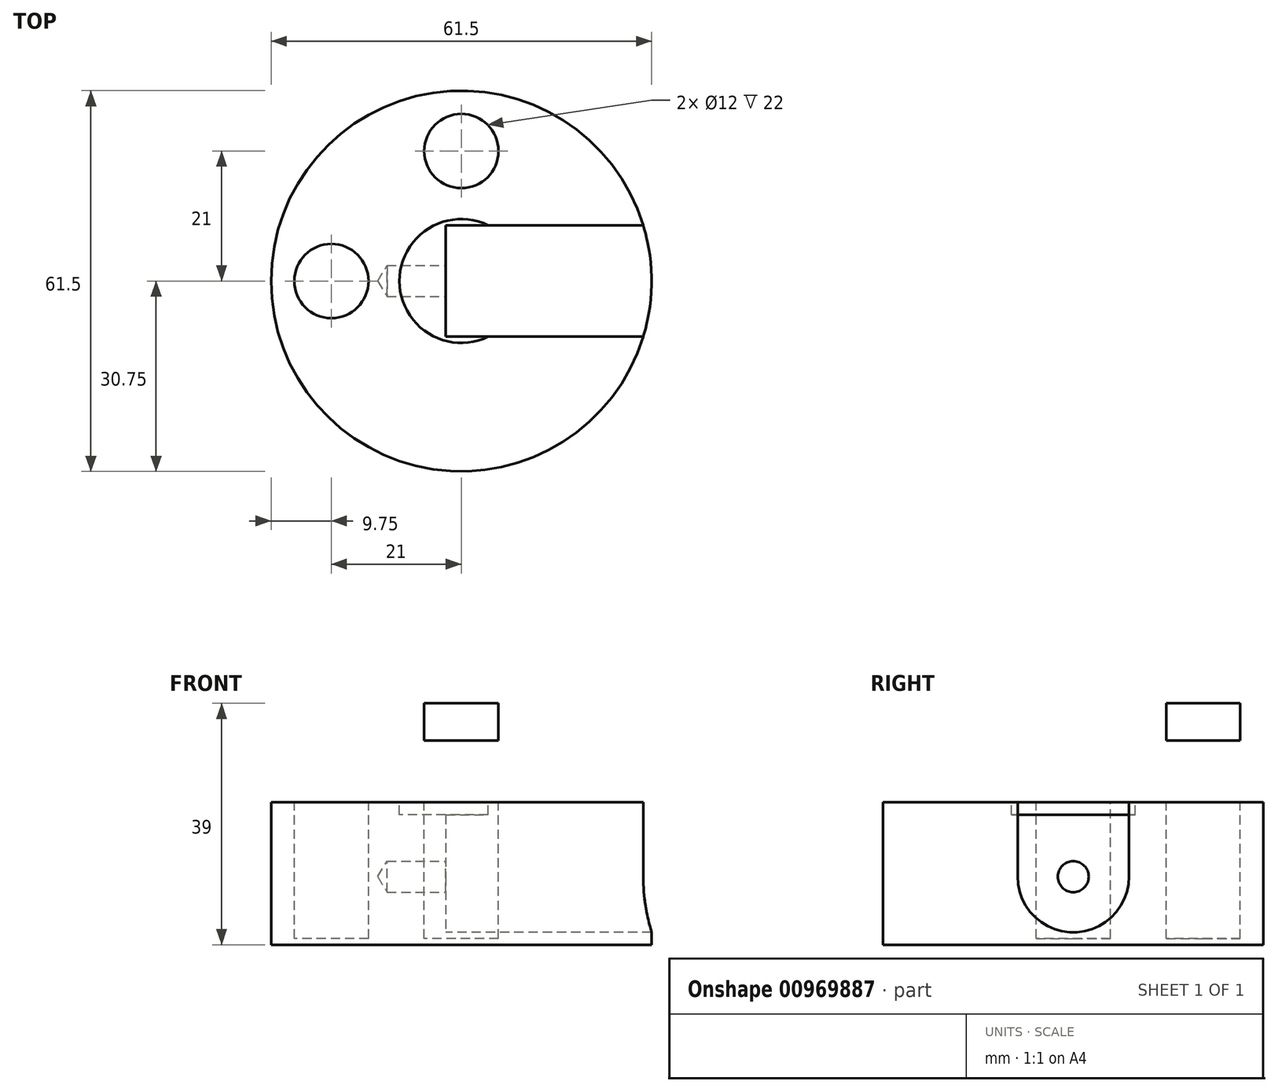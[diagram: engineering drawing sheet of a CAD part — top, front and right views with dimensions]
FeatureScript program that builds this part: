
annotation { "Feature Type Name" : "Feature", "Feature Type Description" : "" }
export const myFeature = defineFeature(function(context is Context, id is Id, definition is map)
    precondition{}
    {
        {
            var Q0;
            Q0=qCreatedBy(makeId("Top.planeOp"),FACE);
            var sketch = newSketch(context, id + "F0", { "sketchPlane" : qUnion([Q0])});
            skCircle(sketch, "E0", {"center": v(0, 0) * mm, "radius": 30.75 * mm});
            skSolve(sketch);
        }
        {
            var Q0;
            Q0=qSketchRegion(id+"F0",true);
            extrude(context, id + "F1", {"entities" : qUnion([Q0]), "depth" : 23 * mm, "offsetDistance" : 25 * mm});
        }
        {
            var Q0;
            Q0=makeQuery(id+"F1.opExtrude","CAP_FACE",FACE,{"disambiguationData":[OSD([sQuery(id+"F0.wireOp",EDGE,"E0")])],"isStart":false});
            var sketch = newSketch(context, id + "F2", { "sketchPlane" : qUnion([Q0])});
            skPoint(sketch, "E1", {"position": v(0, 0) * mm});
            skSolve(sketch);
        }
        {
            var Q0;
            Q0=qCreatedBy(makeId("Right.planeOp"),FACE);
            var sketch = newSketch(context, id + "F3", { "sketchPlane" : qUnion([Q0])});
            skLineSegment(sketch, "E2.bottom", {"start": v(9, 44) * mm, "end": v(-9, 44) * mm});
            skLineSegment(sketch, "E2.top", {"start": v(0, 2) * mm, "end": v(0, 2) * mm});
            skLineSegment(sketch, "E2.left", {"start": v(9, 44) * mm, "end": v(9, 11) * mm});
            skLineSegment(sketch, "E2.right", {"start": v(-9, 44) * mm, "end": v(-9, 11) * mm});
            skPoint(sketch, "E2.middle", {"position": v(0, 23) * mm});
            skPoint(sketch, "E3.visualSharp", {"position": v(-9, 2) * mm});
            skArc(sketch, "E3.filletArc", {"start": v(-9, 11) * mm, "mid": v(-6.36, 4.64) * mm, "end": v(0, 2) * mm});
            skPoint(sketch, "E4.visualSharp", {"position": v(9, 2) * mm});
            skArc(sketch, "E4.filletArc", {"start": v(0, 2) * mm, "mid": v(6.36, 4.64) * mm, "end": v(9, 11) * mm});
            skSolve(sketch);
        }
        {
            var Q0;
            Q0=qSketchRegion(id+"F3",true);
            var Q1;
            Q1=makeQuery(id+"F1.opExtrude","SWEPT_FACE",FACE,{"disambiguationData":[OSD([sQuery(id+"F0.wireOp",EDGE,"E0")])]});
            extrude(context, id + "F4", {"entities" : qUnion([Q0]), "operationType" : NewBodyOperationType.REMOVE, "endBound" : BoundingType.UP_TO_SURFACE, "depth" : 25 * mm, "endBoundEntityFace" : qUnion([Q1]), "offsetDistance" : 25 * mm, "hasSecondDirection" : true, "secondDirectionOppositeDirection" : true, "secondDirectionDepth" : 2.5 * mm});
        }
        {
            var Q0;
            Q0=makeQuery(id+"F2.imprint","IMPRINT",FACE,{"disambiguationData":[TD([[makeQuery(id+"F2.imprint","IMPRINT",EDGE,{"derivedFrom":makeQuery(id+"F1.opExtrude","CAP_EDGE",EDGE,{"disambiguationData":[OSD([sQuery(id+"F0.wireOp",EDGE,"E0")])],"isStart":false})}),1.0]])]});
            var sketch = newSketch(context, id + "F5", { "sketchPlane" : qUnion([Q0])});
            skCircle(sketch, "E5", {"center": v(0, 21) * mm, "radius": 6 * mm});
            skCircle(sketch, "E6", {"center": v(-21, 0) * mm, "radius": 6 * mm});
            skSolve(sketch);
        }
        {
            var Q0;
            Q0=makeQuery(id+"F5.imprint","IMPRINT",FACE,{"disambiguationData":[TD([[makeQuery(id+"F5.imprint","IMPRINT",EDGE,{"derivedFrom":sQuery(id+"F5.wireOp",EDGE,"E5")}),1.0]])]});
            extrude(context, id + "F6", {"entities" : qUnion([Q0]), "operationType" : NewBodyOperationType.REMOVE, "oppositeDirection" : true, "depth" : 22 * mm, "offsetDistance" : 25 * mm});
        }
        {
            var Q0;
            Q0=makeQuery(id+"F5.imprint","IMPRINT",FACE,{"disambiguationData":[TD([[makeQuery(id+"F5.imprint","IMPRINT",EDGE,{"derivedFrom":sQuery(id+"F5.wireOp",EDGE,"E6")}),1.0]])]});
            extrude(context, id + "F7", {"entities" : qUnion([Q0]), "operationType" : NewBodyOperationType.REMOVE, "oppositeDirection" : true, "depth" : 22 * mm, "offsetDistance" : 25 * mm});
        }
        {
            var Q0;
            Q0=makeQuery(id+"F4.boolean.opBoolean","COPY",FACE,{"derivedFrom":makeQuery(id+"F4.opExtrude","CAP_FACE",FACE,{"disambiguationData":[OSD([sQuery(id+"F3.wireOp",EDGE,"E2.bottom"),sQuery(id+"F3.wireOp",EDGE,"E2.left"),sQuery(id+"F3.wireOp",EDGE,"E2.right"),sQuery(id+"F3.wireOp",EDGE,"E3.filletArc"),sQuery(id+"F3.wireOp",EDGE,"E4.filletArc")])],"isStart":true})});
            var sketch = newSketch(context, id + "F8", { "sketchPlane" : qUnion([Q0])});
            skPoint(sketch, "E7", {"position": v(0, 11) * mm});
            skSolve(sketch);
        }
        {
            var Q0;
            Q0=sQuery(id+"F8.wireOp",VERTEX,"E7");
            var Q1;
            Q1=makeQuery(id+"F1.opExtrude","SWEPT_BODY",BODY,{"disambiguationData":[OSD([sQuery(id+"F0.wireOp",EDGE,"E0")])]});
            hole(context, id + "F9", {"style" : HoleStyle.SIMPLE, "endStyle" : HoleEndStyle.BLIND, "standardTappedOrClearance" : lookupTablePath({ "standard" : "ISO", "engagement" : "75%", "pitch" : "1 mm", "size" : "M6", "type" : "Tapped" }), "standardBlindInLast" : lookupTablePath({ "standard" : "ISO", "fit" : "Normal", "engagement" : "75%", "pitch" : "1 mm", "size" : "M6", "type" : "Clearance & tapped" }), "holeDiameter" : 5 * mm, "majorDiameter" : 6 * mm, "showTappedDepth" : true, "holeDepth" : 9.5 * mm, "tappedDepth" : 6.5 * mm, "tapClearance" : 3, "locations" : qUnion([Q0]), "scope" : qUnion([Q1])});
        }
        {
            var Q0;
            Q0=makeQuery(id+"F1.opExtrude","CAP_FACE",FACE,{"disambiguationData":[OSD([sQuery(id+"F0.wireOp",EDGE,"E0")])],"isStart":false});
            var sketch = newSketch(context, id + "F10", { "sketchPlane" : qUnion([Q0])});
            skCircle(sketch, "E8", {"center": v(0, 0) * mm, "radius": 10 * mm});
            skSolve(sketch);
        }
        {
            var Q0;
            Q0=qSketchRegion(id+"F10",true);
            extrude(context, id + "F11", {"entities" : qUnion([Q0]), "operationType" : NewBodyOperationType.REMOVE, "oppositeDirection" : true, "depth" : 2 * mm, "offsetDistance" : 25 * mm});
        }
        {
            var Q0;
            Q0=makeQuery(id+"F1.opExtrude","CAP_FACE",FACE,{"disambiguationData":[OSD([sQuery(id+"F0.wireOp",EDGE,"E0")])],"isStart":false});
            cPlane(context, id + "F12", {"entities" : qUnion([Q0]), "cplaneType" : CPlaneType.OFFSET, "offset" : 10 * mm, "width" : 150 * mm, "height" : 150 * mm});
        }
        {
            var Q0;
            Q0=qCreatedBy(id+"F12.planeOp",FACE);
            var sketch = newSketch(context, id + "F13", { "sketchPlane" : qUnion([Q0])});
            skCircle(sketch, "E9", {"center": v(0, 21) * mm, "radius": 6 * mm});
            skSolve(sketch);
        }
        {
            var Q0;
            Q0=qSketchRegion(id+"F13",true);
            extrude(context, id + "F14", {"entities" : qUnion([Q0]), "depth" : 6 * mm, "offsetDistance" : 25 * mm});
        }
    });
